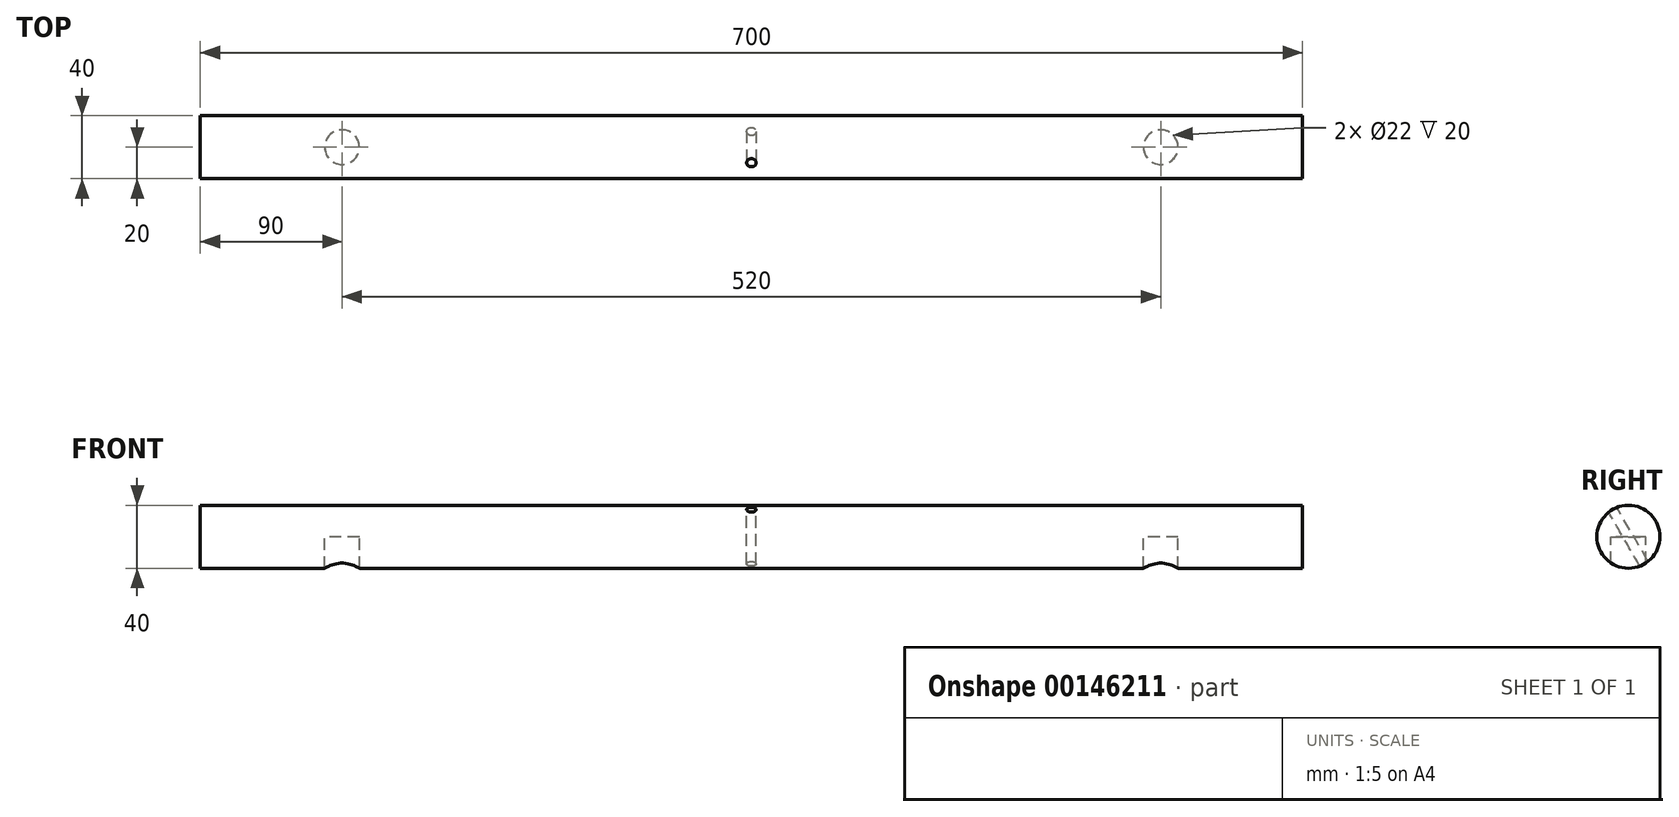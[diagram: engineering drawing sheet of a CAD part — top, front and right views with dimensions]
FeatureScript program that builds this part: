
annotation { "Feature Type Name" : "Feature", "Feature Type Description" : "" }
export const myFeature = defineFeature(function(context is Context, id is Id, definition is map)
    precondition{}
    {
        {
            var Q0;
            Q0=qCreatedBy(makeId("Right.planeOp"),FACE);
            var sketch = newSketch(context, id + "F0", { "sketchPlane" : qUnion([Q0])});
            skCircle(sketch, "E0", {"center": v(0, 0) * mm, "radius": 20 * mm});
            skLineSegment(sketch, "E1", {"start": v(0, 0) * mm, "end": v(-10, 17.32) * mm});
            skLineSegment(sketch, "E2", {"start": v(-1.34, 22.32) * mm, "end": v(-18.66, 12.32) * mm});
            skSolve(sketch);
        }
        {
            var Q0;
            Q0=qSketchRegion(id+"F0",true);
            extrude(context, id + "F1", {"entities" : qUnion([Q0]), "depth" : 700 * mm, "symmetric" : true});
        }
        {
            var Q0;
            Q0=qCreatedBy(makeId("Top.planeOp"),FACE);
            var sketch = newSketch(context, id + "F2", { "sketchPlane" : qUnion([Q0])});
            skCircle(sketch, "E3", {"center": v(-260, 0) * mm, "radius": 11 * mm});
            skCircle(sketch, "E4.MirrorC", {"center": v(260, 0) * mm, "radius": 11 * mm});
            skSolve(sketch);
        }
        {
            var Q0;
            Q0=qSketchRegion(id+"F2",true);
            extrude(context, id + "F3", {"entities" : qUnion([Q0]), "operationType" : NewBodyOperationType.REMOVE, "oppositeDirection" : true, "depth" : 25.4 * mm});
        }
        {
            var Q0;
            Q0=sQuery(id+"F0.wireOp",EDGE,"E2");
            var Q1;
            Q1=makeQuery(id+"F1.opExtrude","SWEPT_FACE",FACE,{"disambiguationData":[OSD([sQuery(id+"F0.wireOp",EDGE,"E0")])]});
            cPlane(context, id + "F4", {"entities" : qUnion([Q0, Q1]), "cplaneType" : CPlaneType.LINE_ANGLE, "offset" : 25.4 * mm, "angle" : 0 * degree, "width" : 152.4 * mm, "height" : 152.4 * mm});
        }
        {
            var Q0;
            Q0=qCreatedBy(id+"F4.planeOp",FACE);
            var sketch = newSketch(context, id + "F5", { "sketchPlane" : qUnion([Q0])});
            skCircle(sketch, "E5", {"center": v(0, 0) * mm, "radius": 3 * mm});
            skSolve(sketch);
        }
        {
            var Q0;
            Q0=makeQuery(id+"F5.imprint","IMPRINT",FACE,{"disambiguationData":[TD([[makeQuery(id+"F5.imprint","IMPRINT",EDGE,{"derivedFrom":sQuery(id+"F5.wireOp",EDGE,"E5")}),1.0]])]});
            var Q1;
            Q1=sQuery(id+"F5.wireOp",EDGE,"E5");
            extrude(context, id + "F6", {"entities" : qUnion([Q0]), "operationType" : NewBodyOperationType.REMOVE, "surfaceEntities" : qUnion([Q1]), "endBound" : BoundingType.THROUGH_ALL, "depth" : 25.4 * mm});
        }
    });
